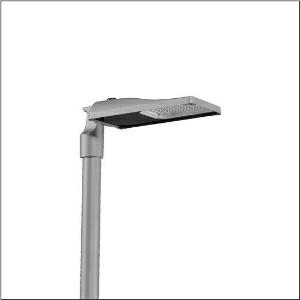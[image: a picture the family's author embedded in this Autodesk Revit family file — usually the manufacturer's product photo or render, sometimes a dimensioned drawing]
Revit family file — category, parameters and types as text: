
# Revit family: streetlight_sl_31_mini___st1_0a_5xh2d31s08ha_0250
name_source: partatom
category: Lighting Fixtures
units: mm (PartAtom-declared; Revit-internal decimal feet)

## family parameters
Cut with Voids When Loaded = No
Host = Face
Light Source = No
Part Type = Normal
Room Calculation Point = No
Round Connector Dimension = Use Diameter
Shared = No

## types (1)
- --- (1 x LED, 9230 lm, 68.3 W, 3000K)
    Apparent Load = 68 VA
    CIE Flux Codes = 37 72 97 100 100
    Color Rendering = 70
    Color Temperature = 3000K
    Default Elevation = 1800 mm
    Description = Streetlight SL 31 mini D4i, Desk-Remote mast luminaire for post-top, side-entry; light control with lens of PMMA; light distribution: ST1.0a, direct asymmetric distribution, for standard-compliant lighting for roads and squares; LED: luminous flux: 9.230lm, light colour: 730, colour temperature: 3000K; luminous efficacy: 135,1lm/W; control: pre-setting: logarithmic dimming characteristic, flexible luminous flux parameterisation, time-dependent luminous flux control, constant luminous flux control, power reduction, intelligent temperature release in ECG and LED module, overheat protection; luminaire housing, of diecast aluminium, Siteco® metallic grey (DB 702S), corrosivity category C5 high according to DIN EN ISO 12944; cover of toughened safety glass, transparent, mast flange of diecast aluminium, Siteco® metallic grey (DB 702S), spigot size: 76/60mm, mast flange included unmounted; with cable H07RN-F 2x 1.5mm², cable length: 8,5m, connection cable pre-assembled; mains connection: 220..240V, AC, 50/60Hz; power consumption (at start of service life): 68,3W / (at end of service life): 74,5W / (with reduced operation 50%): 29,5W; protection rating (complete): IP66; insulation class (complete): insulation class II (safety insulation); impact resistance: IK10; certification: CE, ENEC, ENEC+, VDE, UKCA, ZD4i; permissible operating ambient temperature for outdoor applications: -40..+50°C; packaging unit: 1 piece

Light Distribution: ST1.0a
    Height = 76 mm
    Lamp = 1 x LED
    Lamp Light Flux = 9230 lm
    Lamp Power = 68.3 W
    Lamp count = 1
    Length = 547 mm
    Luminous efficacy = 135 lm/W
    Manufacturer = Siteco
    ModVariant = No
    Model = 5XH2D31S08HA
    Number of Poles = 1
    OnlyDefault = Yes
    Power Factor = 1
    Product Name = Streetlight SL 31 mini | ST1.0a
    Product group = mast luminaire | pylon top
    ProductGroupID = 6100
    Protection Class = Protection class II
    Protection Degree = IP 66
    RLX_Detail_Level = 1
    RLX_Emergency_Light_Flux = 0 lm
    RLX_Emergency_Type = 0
    RLX_Emergency_Type_DB = No
    RlxData = <blob elided: 39381 chars, md5=ba80317c>
    Socket = socket
    Standby Power = 0 W
    System Light Flux = 9230 lm
    System Power = 68 W
    Type Comments = factory setting: luminous flux: 100 % | dim-lin: 254 | 692 mA
    Type Image = l_1300330.jpg
    URL = http://relux.com
    VarID = @adj_019569
    Voltage = 0 V
    Weight = 0.00 kg
    Width = 265 mm

## geometry (parser evidence)
native form markers: Blend x4, Sweep x11
no freeform markers — native parametric forms only
